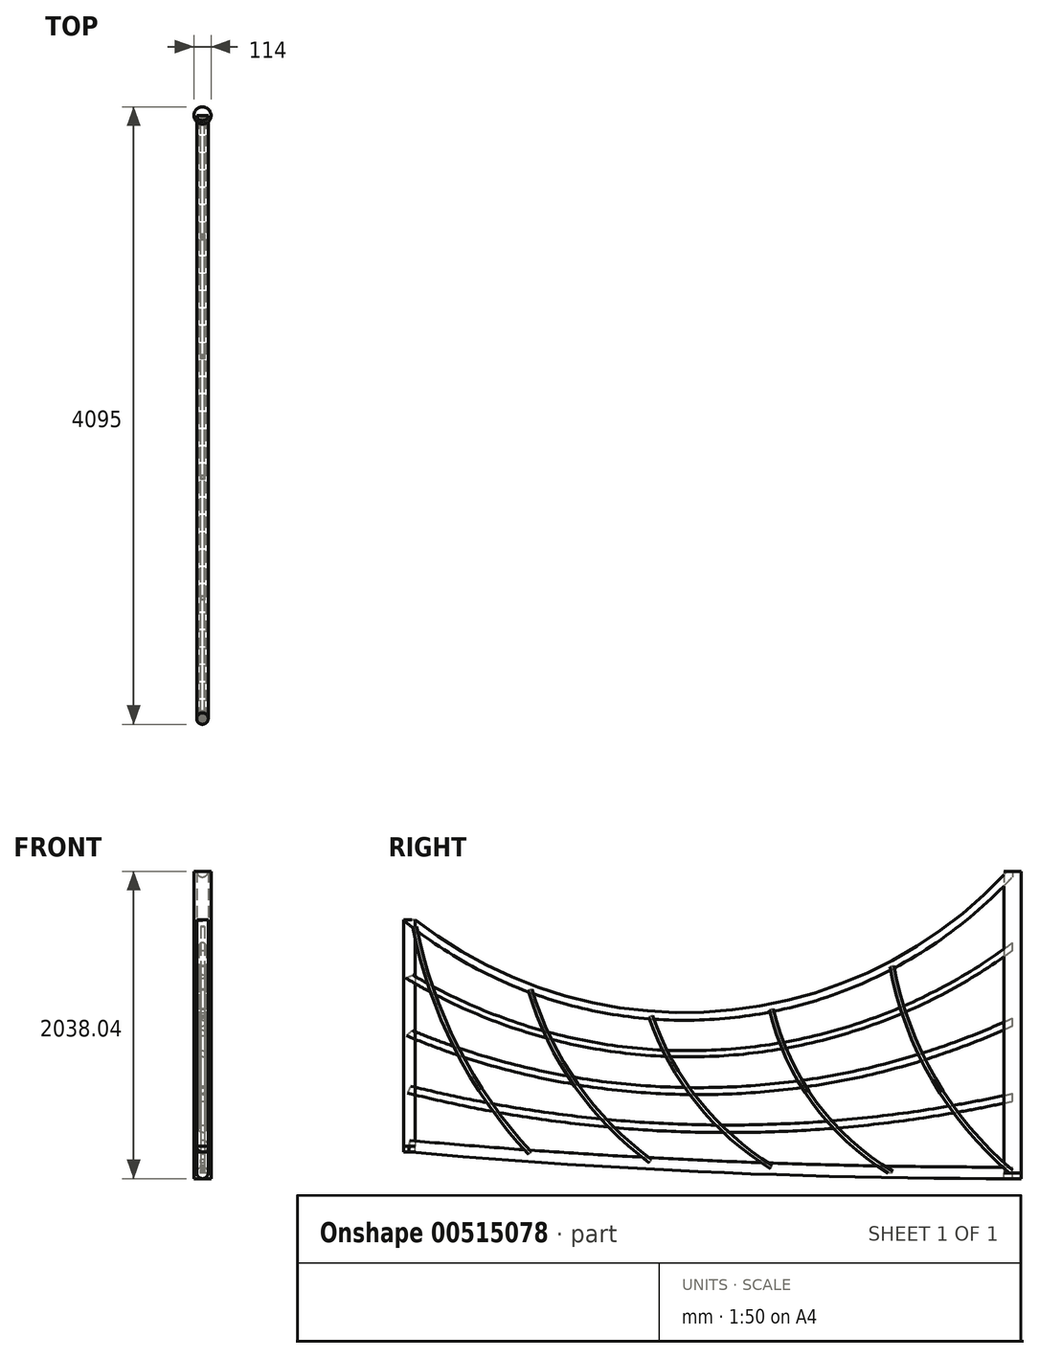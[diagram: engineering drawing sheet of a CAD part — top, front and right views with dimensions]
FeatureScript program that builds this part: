
annotation { "Feature Type Name" : "Feature", "Feature Type Description" : "" }
export const myFeature = defineFeature(function(context is Context, id is Id, definition is map)
    precondition{}
    {
        {
            var Q0;
            Q0=qCreatedBy(makeId("Right.planeOp"),FACE);
            var sketch = newSketch(context, id + "F0", { "sketchPlane" : qUnion([Q0])});
            skLineSegment(sketch, "E0.top", {"start": v(0, 2000) * mm, "end": v(-4000, 2000) * mm});
            skLineSegment(sketch, "E0.left", {"start": v(0, 0) * mm, "end": v(0, 2000) * mm});
            skLineSegment(sketch, "E0.right", {"start": v(-4000, 0) * mm, "end": v(-4000, 2000) * mm});
            skPoint(sketch, "E1", {"position": v(-4000, 177) * mm});
            skPoint(sketch, "E2", {"position": v(-4000, 552) * mm});
            skPoint(sketch, "E3", {"position": v(-4000, 927) * mm});
            skPoint(sketch, "E4", {"position": v(-4000, 1302) * mm});
            skPoint(sketch, "E5", {"position": v(-4000, 1677) * mm});
            skPoint(sketch, "E6", {"position": v(0, 500) * mm});
            skPoint(sketch, "E7", {"position": v(0, 1000) * mm});
            skPoint(sketch, "E8", {"position": v(0, 1500) * mm});
            skPoint(sketch, "E9", {"position": v(0, 2000) * mm});
            skArc(sketch, "E10", {"start": v(-4000, 177) * mm, "mid": v(-2002.01, 42.98) * mm, "end": v(0, 0) * mm});
            skPoint(sketch, "E11", {"position": v(-2000, 1042.9) * mm});
            skPoint(sketch, "E11.positionSnap0", {"position": v(-2000, 0) * mm});
            skPoint(sketch, "E12", {"position": v(-2000, 792.9) * mm});
            skPoint(sketch, "E13", {"position": v(-2000, 542.9) * mm});
            skPoint(sketch, "E14", {"position": v(-2000, 292.9) * mm});
            skPoint(sketch, "E15", {"position": v(-2000, 42.9) * mm});
            skArc(sketch, "E16", {"start": v(-4000, 552) * mm, "mid": v(-2003.03, 292.93) * mm, "end": v(0, 500) * mm});
            skArc(sketch, "E17", {"start": v(-4000, 927) * mm, "mid": v(-1992.33, 543.02) * mm, "end": v(0, 1000) * mm});
            skArc(sketch, "E18", {"start": v(-4000, 1302) * mm, "mid": v(-1969.97, 794.25) * mm, "end": v(0, 1500) * mm});
            skArc(sketch, "E19", {"start": v(-4000, 1677) * mm, "mid": v(-1936.11, 1047.35) * mm, "end": v(0, 2000) * mm});
            skSolve(sketch);
        }
        {
            var Q0;
            Q0=qCreatedBy(makeId("Front.planeOp"),FACE);
            var sketch = newSketch(context, id + "F1", { "sketchPlane" : qUnion([Q0])});
            skCircle(sketch, "E20", {"center": v(0, 500) * mm, "radius": 25.5 * mm});
            skCircle(sketch, "E21", {"center": v(0, 1000) * mm, "radius": 25.5 * mm});
            skCircle(sketch, "E22", {"center": v(0, 1500) * mm, "radius": 25.5 * mm});
            skCircle(sketch, "E23", {"center": v(0, 2000) * mm, "radius": 38 * mm});
            skCircle(sketch, "E24", {"center": v(0, 0) * mm, "radius": 38 * mm});
            skSolve(sketch);
        }
        {
            var Q0;
            Q0=makeQuery(id+"F1.imprint","IMPRINT",FACE,{"disambiguationData":[TD([[makeQuery(id+"F1.imprint","IMPRINT",EDGE,{"derivedFrom":sQuery(id+"F1.wireOp",EDGE,"E24")}),1.0]])]});
            var Q1;
            Q1=sQuery(id+"F0.wireOp",EDGE,"E10");
            sweep(context, id + "F2", {"profiles" : qUnion([Q0]), "path" : qUnion([Q1])});
        }
        {
            var Q0;
            Q0=makeQuery(id+"F1.imprint","IMPRINT",FACE,{"disambiguationData":[TD([[makeQuery(id+"F1.imprint","IMPRINT",EDGE,{"derivedFrom":sQuery(id+"F1.wireOp",EDGE,"E20")}),1.0]])]});
            var Q1;
            Q1=sQuery(id+"F0.wireOp",EDGE,"E16");
            sweep(context, id + "F3", {"profiles" : qUnion([Q0]), "path" : qUnion([Q1])});
        }
        {
            var Q0;
            Q0=makeQuery(id+"F1.imprint","IMPRINT",FACE,{"disambiguationData":[TD([[makeQuery(id+"F1.imprint","IMPRINT",EDGE,{"derivedFrom":sQuery(id+"F1.wireOp",EDGE,"E21")}),1.0]])]});
            var Q1;
            Q1=sQuery(id+"F0.wireOp",EDGE,"E17");
            sweep(context, id + "F4", {"profiles" : qUnion([Q0]), "path" : qUnion([Q1])});
        }
        {
            var Q0;
            Q0=makeQuery(id+"F1.imprint","IMPRINT",FACE,{"disambiguationData":[TD([[makeQuery(id+"F1.imprint","IMPRINT",EDGE,{"derivedFrom":sQuery(id+"F1.wireOp",EDGE,"E22")}),1.0]])]});
            var Q1;
            Q1=sQuery(id+"F0.wireOp",EDGE,"E18");
            sweep(context, id + "F5", {"profiles" : qUnion([Q0]), "path" : qUnion([Q1])});
        }
        {
            var Q0;
            Q0=makeQuery(id+"F1.imprint","IMPRINT",FACE,{"disambiguationData":[TD([[makeQuery(id+"F1.imprint","IMPRINT",EDGE,{"derivedFrom":sQuery(id+"F1.wireOp",EDGE,"E23")}),1.0]])]});
            var Q1;
            Q1=sQuery(id+"F0.wireOp",EDGE,"E19");
            sweep(context, id + "F6", {"profiles" : qUnion([Q0]), "path" : qUnion([Q1])});
        }
        {
            var Q0;
            Q0=qCreatedBy(makeId("Top.planeOp"),FACE);
            var sketch = newSketch(context, id + "F7", { "sketchPlane" : qUnion([Q0])});
            skCircle(sketch, "E25", {"center": v(0, 0) * mm, "radius": 57 * mm});
            skSolve(sketch);
        }
        {
            var Q0;
            Q0=makeQuery(id+"F7.imprint","IMPRINT",FACE,{"disambiguationData":[TD([[makeQuery(id+"F7.imprint","IMPRINT",EDGE,{"derivedFrom":sQuery(id+"F7.wireOp",EDGE,"E25")}),1.0]])]});
            extrude(context, id + "F8", {"entities" : qUnion([Q0]), "depth" : 2000 * mm, "offsetDistance" : 25 * mm});
        }
        {
            var Q0;
            Q0=makeQuery(id+"F1.imprint","IMPRINT",FACE,{"disambiguationData":[TD([[makeQuery(id+"F1.imprint","IMPRINT",EDGE,{"derivedFrom":sQuery(id+"F1.wireOp",EDGE,"E23")}),1.0]])]});
            var sketch = newSketch(context, id + "F9", { "sketchPlane" : qUnion([Q0])});
            skLineSegment(sketch, "E26.0", {"start": v(-57, 2000) * mm, "end": v(57, 2000) * mm});
            skLineSegment(sketch, "E27.top", {"start": v(-57, 2042.72) * mm, "end": v(57, 2042.72) * mm});
            skLineSegment(sketch, "E27.left", {"start": v(-57, 2000) * mm, "end": v(-57, 2042.72) * mm});
            skLineSegment(sketch, "E27.right", {"start": v(57, 2000) * mm, "end": v(57, 2042.72) * mm});
            skSolve(sketch);
        }
        {
            var Q0;
            {var subQ0=sQuery(id+"F9.wireOp",EDGE,"E26.0");var subQ1=makeQuery(id+"F1.imprint","IMPRINT",EDGE,{"derivedFrom":sQuery(id+"F1.wireOp",EDGE,"E23")});var subQ2=makeQuery(id+"F9.imprint","INTERSECT",VERTEX,{"disambiguationData":[OD(0.0)],"derivedFrom":[subQ1,subQ0]});Q0=makeQuery(id+"F9.imprint","IMPRINT",FACE,{"disambiguationData":[TD([[makeQuery(id+"F9.imprint","IMPRINT",EDGE,{"disambiguationData":[TD([[subQ2,-1.0]])],"derivedFrom":subQ0}),1.0]])]});}
            extrude(context, id + "F10", {"entities" : qUnion([Q0]), "operationType" : NewBodyOperationType.REMOVE, "depth" : 50 * mm, "offsetDistance" : 25 * mm});
        }
        {
            var Q0;
            Q0=makeQuery(id+"F8.opExtrude","CAP_FACE",FACE,{"disambiguationData":[OSD([sQuery(id+"F7.wireOp",EDGE,"E25")])],"isStart":true});
            extrude(context, id + "F11", {"entities" : qUnion([Q0]), "depth" : 38 * mm, "offsetDistance" : 25 * mm});
        }
        {
            var Q0;
            Q0=qCreatedBy(makeId("Top.planeOp"),FACE);
            cPlane(context, id + "F12", {"entities" : qUnion([Q0]), "cplaneType" : CPlaneType.OFFSET, "offset" : 178 * mm, "width" : 150 * mm, "height" : 150 * mm});
        }
        {
            var Q0;
            Q0=qCreatedBy(id+"F12.planeOp",FACE);
            var sketch = newSketch(context, id + "F13", { "sketchPlane" : qUnion([Q0])});
            skCircle(sketch, "E28", {"center": v(0, -4000) * mm, "radius": 38 * mm});
            skSolve(sketch);
        }
        {
            var Q0;
            Q0=makeQuery(id+"F13.imprint","IMPRINT",FACE,{"disambiguationData":[TD([[makeQuery(id+"F13.imprint","IMPRINT",EDGE,{"derivedFrom":sQuery(id+"F13.wireOp",EDGE,"E28")}),1.0]])]});
            extrude(context, id + "F14", {"entities" : qUnion([Q0]), "depth" : 1500 * mm, "offsetDistance" : 25 * mm});
        }
        {
            var Q0;
            Q0=makeQuery(id+"F14.opExtrude","CAP_FACE",FACE,{"disambiguationData":[OSD([sQuery(id+"F13.wireOp",EDGE,"E28")])],"isStart":true});
            extrude(context, id + "F15", {"entities" : qUnion([Q0]), "depth" : 40 * mm, "offsetDistance" : 25 * mm});
        }
        {
            var Q0;
            Q0=qCreatedBy(makeId("Right.planeOp"),FACE);
            var sketch = newSketch(context, id + "F16", { "sketchPlane" : qUnion([Q0])});
            skLineSegment(sketch, "E29.bottom", {"start": v(0, 0) * mm, "end": v(-4000, 0) * mm});
            skLineSegment(sketch, "E29.left", {"start": v(0, 0) * mm, "end": v(0, 2000) * mm});
            skPoint(sketch, "E30", {"position": v(-800, 0) * mm});
            skPoint(sketch, "E31", {"position": v(-1600, 0) * mm});
            skPoint(sketch, "E32", {"position": v(-2400, 0) * mm});
            skPoint(sketch, "E33", {"position": v(-3200, 0) * mm});
            skArc(sketch, "E34", {"start": v(-800, 1370.14) * mm, "mid": v(-518.57, 615.84) * mm, "end": v(0, 0) * mm});
            skArc(sketch, "E35", {"start": v(-1600, 1085) * mm, "mid": v(-1309.74, 461.58) * mm, "end": v(-800, 0) * mm});
            skArc(sketch, "E36", {"start": v(-2400, 1038.39) * mm, "mid": v(-2085.67, 470.5) * mm, "end": v(-1600, 39.9) * mm});
            skArc(sketch, "E37", {"start": v(-3200, 1215.38) * mm, "mid": v(-2892.62, 581.07) * mm, "end": v(-2400, 76.92) * mm});
            skArc(sketch, "E38", {"start": v(-3964.44, 1633.04) * mm, "mid": v(-3687.4, 828.04) * mm, "end": v(-3200, 130.02) * mm});
            skArc(sketch, "E39.0", {"start": v(-3977.2, 1630.55) * mm, "mid": v(-3698.98, 822.14) * mm, "end": v(-3209.52, 121.17) * mm});
            skArc(sketch, "E40.0", {"start": v(-3951.68, 1635.52) * mm, "mid": v(-3675.8, 833.93) * mm, "end": v(-3190.48, 138.87) * mm});
            skArc(sketch, "E41.0", {"start": v(-3212.46, 1211.66) * mm, "mid": v(-2903.25, 573.6) * mm, "end": v(-2407.72, 66.46) * mm});
            skArc(sketch, "E42.0", {"start": v(-3187.54, 1219.1) * mm, "mid": v(-2881.98, 588.54) * mm, "end": v(-2392.28, 87.38) * mm});
            skArc(sketch, "E43.0", {"start": v(-2412.27, 1034.1) * mm, "mid": v(-2095.82, 462.38) * mm, "end": v(-1606.86, 28.85) * mm});
            skArc(sketch, "E44.0", {"start": v(-2387.73, 1042.67) * mm, "mid": v(-2075.53, 478.63) * mm, "end": v(-1593.14, 50.94) * mm});
            skArc(sketch, "E45.0", {"start": v(-1612.64, 1081.96) * mm, "mid": v(-1320.2, 453.87) * mm, "end": v(-806.64, -11.18) * mm});
            skArc(sketch, "E46.0", {"start": v(-1587.36, 1088.04) * mm, "mid": v(-1299.28, 469.3) * mm, "end": v(-793.36, 11.18) * mm});
            skArc(sketch, "E47.0", {"start": v(-812.78, 1367.74) * mm, "mid": v(-529.8, 609.28) * mm, "end": v(-8.37, -9.95) * mm});
            skArc(sketch, "E48.0", {"start": v(-787.22, 1372.54) * mm, "mid": v(-507.34, 622.4) * mm, "end": v(8.37, 9.95) * mm});
            skLineSegment(sketch, "E49", {"start": v(-787.22, 1372.54) * mm, "end": v(-812.78, 1367.74) * mm});
            skLineSegment(sketch, "E50", {"start": v(-1587.36, 1088.04) * mm, "end": v(-1612.64, 1081.96) * mm});
            skLineSegment(sketch, "E51", {"start": v(-2387.73, 1042.67) * mm, "end": v(-2412.27, 1034.1) * mm});
            skLineSegment(sketch, "E52", {"start": v(-3187.54, 1219.1) * mm, "end": v(-3212.46, 1211.66) * mm});
            skLineSegment(sketch, "E53", {"start": v(-3951.68, 1635.52) * mm, "end": v(-3977.2, 1630.55) * mm});
            skLineSegment(sketch, "E54", {"start": v(-3190.48, 138.87) * mm, "end": v(-3209.52, 121.17) * mm});
            skLineSegment(sketch, "E55", {"start": v(-2407.72, 66.46) * mm, "end": v(-2392.28, 87.38) * mm});
            skLineSegment(sketch, "E56", {"start": v(-1606.86, 28.85) * mm, "end": v(-1593.14, 50.94) * mm});
            skLineSegment(sketch, "E57", {"start": v(-806.64, -11.18) * mm, "end": v(-793.36, 11.18) * mm});
            skLineSegment(sketch, "E58", {"start": v(-8.37, -9.95) * mm, "end": v(8.37, 9.95) * mm});
            skSolve(sketch);
        }
        {
            var Q0;
            {var subQ0=sQuery(id+"F16.wireOp",EDGE,"E34");Q0=makeQuery(id+"F16.imprint","IMPRINT",FACE,{"disambiguationData":[TD([[makeQuery(id+"F16.imprint","IMPRINT",EDGE,{"derivedFrom":subQ0}),1.0]])]});}
            var Q1;
            {var subQ0=sQuery(id+"F16.wireOp",EDGE,"E34");Q1=makeQuery(id+"F16.imprint","IMPRINT",FACE,{"disambiguationData":[TD([[makeQuery(id+"F16.imprint","IMPRINT",EDGE,{"derivedFrom":subQ0}),-1.0]])]});}
            var Q2;
            {var subQ0=sQuery(id+"F16.wireOp",EDGE,"E35");Q2=makeQuery(id+"F16.imprint","IMPRINT",FACE,{"disambiguationData":[TD([[makeQuery(id+"F16.imprint","IMPRINT",EDGE,{"derivedFrom":subQ0}),1.0]])]});}
            var Q3;
            {var subQ0=sQuery(id+"F16.wireOp",EDGE,"E35");Q3=makeQuery(id+"F16.imprint","IMPRINT",FACE,{"disambiguationData":[TD([[makeQuery(id+"F16.imprint","IMPRINT",EDGE,{"derivedFrom":subQ0}),-1.0]])]});}
            var Q4;
            {var subQ0=sQuery(id+"F16.wireOp",EDGE,"E36");Q4=makeQuery(id+"F16.imprint","IMPRINT",FACE,{"disambiguationData":[TD([[makeQuery(id+"F16.imprint","IMPRINT",EDGE,{"derivedFrom":subQ0}),1.0]])]});}
            var Q5;
            {var subQ0=sQuery(id+"F16.wireOp",EDGE,"E36");Q5=makeQuery(id+"F16.imprint","IMPRINT",FACE,{"disambiguationData":[TD([[makeQuery(id+"F16.imprint","IMPRINT",EDGE,{"derivedFrom":subQ0}),-1.0]])]});}
            var Q6;
            {var subQ0=sQuery(id+"F16.wireOp",EDGE,"E37");Q6=makeQuery(id+"F16.imprint","IMPRINT",FACE,{"disambiguationData":[TD([[makeQuery(id+"F16.imprint","IMPRINT",EDGE,{"derivedFrom":subQ0}),1.0]])]});}
            var Q7;
            {var subQ0=sQuery(id+"F16.wireOp",EDGE,"E37");Q7=makeQuery(id+"F16.imprint","IMPRINT",FACE,{"disambiguationData":[TD([[makeQuery(id+"F16.imprint","IMPRINT",EDGE,{"derivedFrom":subQ0}),-1.0]])]});}
            var Q8;
            {var subQ0=sQuery(id+"F16.wireOp",EDGE,"E38");Q8=makeQuery(id+"F16.imprint","IMPRINT",FACE,{"disambiguationData":[TD([[makeQuery(id+"F16.imprint","IMPRINT",EDGE,{"derivedFrom":subQ0}),1.0]])]});}
            var Q9;
            {var subQ0=sQuery(id+"F16.wireOp",EDGE,"E38");Q9=makeQuery(id+"F16.imprint","IMPRINT",FACE,{"disambiguationData":[TD([[makeQuery(id+"F16.imprint","IMPRINT",EDGE,{"derivedFrom":subQ0}),-1.0]])]});}
            extrude(context, id + "F17", {"entities" : qUnion([Q0, Q1, Q2, Q3, Q4, Q5, Q6, Q7, Q8, Q9]), "endBound" : BoundingType.SYMMETRIC, "depth" : 25 * mm, "offsetDistance" : 25 * mm});
        }
    });
